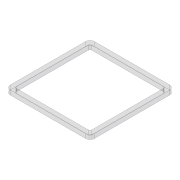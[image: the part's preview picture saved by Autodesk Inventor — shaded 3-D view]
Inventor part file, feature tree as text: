
AUTODESK INVENTOR PART (.ipt)
format: ipt  version: 2020 (Build 240168000, 168)  size: 115,200 bytes
history: native  units: mm
features: sketch x3, extrude x2, fillet x2
ambient origin geometry x8: Origin, YZ Plane, XZ Plane, XY Plane, X Axis, Y Axis, Z Axis, Center Point
bodies: Solid1 (feature_tree)
feature tree (7):
  extrude  "Extrusion1"  Depth=95.0mm
  extrude  "Extrusion2"  Depth=5.0mm
  fillet  "Fillet1"  Radius=5.0mm
  sketch  "Sketch3"  dims[d7=5.0mm d8=5.0mm d9=0.0mm d10=5.0mm d11=2.5mm d12=2.5mm d13=2.5mm d14=2.5mm d15=2.0mm]
  fillet  "Fillet2"  Radius=5.0mm
  sketch  "Sketch1"  dims[d0=95.0mm d1=95.0mm]
  sketch  "Sketch2"  dims[d2=5.0mm d3=0.0mm d4=5.0mm d5=5.0mm d6=5.0mm]
